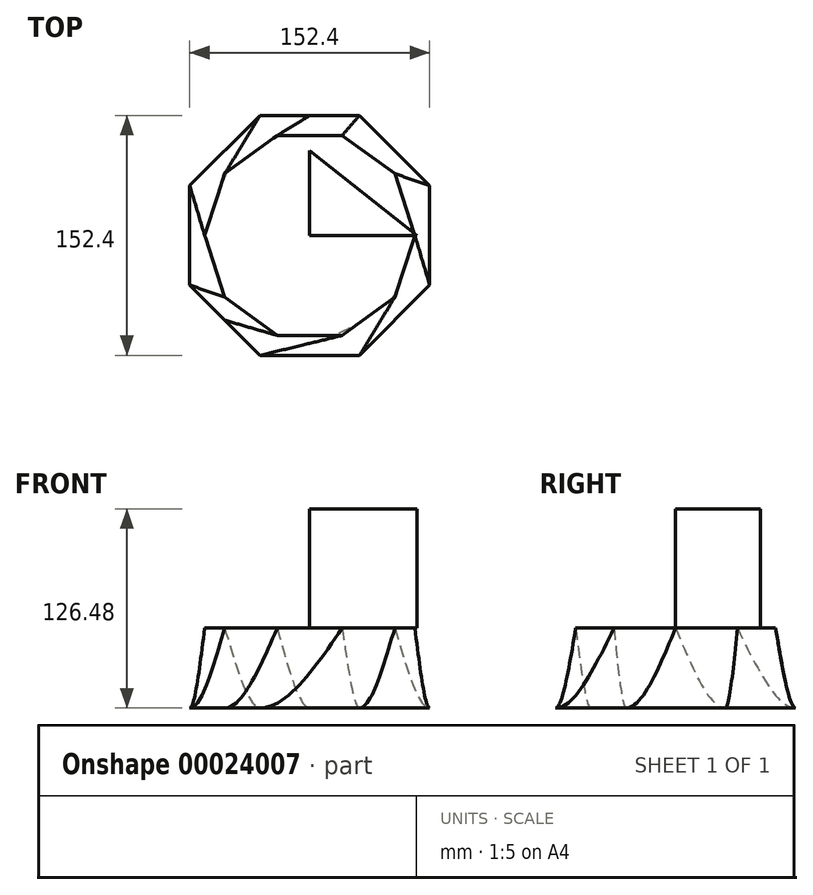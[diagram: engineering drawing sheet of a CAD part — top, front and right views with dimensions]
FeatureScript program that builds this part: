
annotation { "Feature Type Name" : "Feature", "Feature Type Description" : "" }
export const myFeature = defineFeature(function(context is Context, id is Id, definition is map)
    precondition{}
    {
        {
            var Q0;
            Q0=qCreatedBy(makeId("Top.planeOp"),FACE);
            var sketch = newSketch(context, id + "F0", { "sketchPlane" : qUnion([Q0])});
            skCircle(sketch, "E0.cCircle", {"center": v(0, 0) * mm, "radius": 76.2 * mm, "construction": true});
            skLineSegment(sketch, "E0.0", {"start": v(31.56, 76.2) * mm, "end": v(76.2, 31.56) * mm});
            skLineSegment(sketch, "E0.1", {"start": v(76.2, 31.56) * mm, "end": v(76.2, -31.56) * mm});
            skLineSegment(sketch, "E0.2", {"start": v(76.2, -31.56) * mm, "end": v(31.56, -76.2) * mm});
            skLineSegment(sketch, "E0.3", {"start": v(31.56, -76.2) * mm, "end": v(-31.56, -76.2) * mm});
            skLineSegment(sketch, "E0.4", {"start": v(-31.56, -76.2) * mm, "end": v(-76.2, -31.56) * mm});
            skLineSegment(sketch, "E0.5", {"start": v(-76.2, -31.56) * mm, "end": v(-76.2, 31.56) * mm});
            skLineSegment(sketch, "E0.6", {"start": v(-76.2, 31.56) * mm, "end": v(-31.56, 76.2) * mm});
            skLineSegment(sketch, "E0.7", {"start": v(-31.56, 76.2) * mm, "end": v(31.56, 76.2) * mm});
            skPoint(sketch, "E0.0.midPoint", {"position": v(53.88, 53.88) * mm});
            skSolve(sketch);
        }
        {
            var Q0;
            Q0 = qSketchRegion(id + "F0", true);
            var Q1;
            Q1=sQuery(id+"F0.wireOp",EDGE,"E0.6");
            var Q2;
            Q2=sQuery(id+"F0.wireOp",EDGE,"E0.7");
            var Q3;
            Q3=sQuery(id+"F0.wireOp",EDGE,"E0.0");
            var Q4;
            Q4=sQuery(id+"F0.wireOp",EDGE,"E0.5");
            var Q5;
            Q5=sQuery(id+"F0.wireOp",EDGE,"E0.4");
            var Q6;
            Q6=sQuery(id+"F0.wireOp",EDGE,"E0.3");
            var Q7;
            Q7=sQuery(id+"F0.wireOp",EDGE,"E0.2");
            var Q8;
            Q8=sQuery(id+"F0.wireOp",EDGE,"E0.1");
            extrude(context, id + "F1", {"entities" : qUnion([Q0]), "bodyType" : ToolBodyType.SURFACE, "surfaceEntities" : qUnion([Q1, Q2, Q3, Q4, Q5, Q6, Q7, Q8]), "oppositeDirection" : true, "depth" : 55.84 * mm, "hasDraft" : true, "draftAngle" : 3 * degree});
        }
        {
            var Q0;
            Q0=qCreatedBy(makeId("Top.planeOp"),FACE);
            cPlane(context, id + "F2", {"entities" : qUnion([Q0]), "cplaneType" : CPlaneType.OFFSET, "offset" : 50.8 * mm, "width" : 152.4 * mm, "height" : 152.4 * mm});
        }
        {
            var Q0;
            Q0=qCreatedBy(id+"F2.planeOp",FACE);
            var sketch = newSketch(context, id + "F3", { "sketchPlane" : qUnion([Q0])});
            skCircle(sketch, "E1.cCircle", {"center": v(0, 0) * mm, "radius": 63.5 * mm, "construction": true});
            skLineSegment(sketch, "E1.0", {"start": v(-66.77, 0) * mm, "end": v(-54.02, 39.25) * mm});
            skLineSegment(sketch, "E1.1", {"start": v(-54.02, 39.25) * mm, "end": v(-20.63, 63.5) * mm});
            skLineSegment(sketch, "E1.2", {"start": v(-20.63, 63.5) * mm, "end": v(20.63, 63.5) * mm});
            skLineSegment(sketch, "E1.3", {"start": v(20.63, 63.5) * mm, "end": v(54.02, 39.25) * mm});
            skLineSegment(sketch, "E1.4", {"start": v(54.02, 39.25) * mm, "end": v(66.77, 0) * mm});
            skLineSegment(sketch, "E1.5", {"start": v(66.77, 0) * mm, "end": v(54.02, -39.25) * mm});
            skLineSegment(sketch, "E1.6", {"start": v(54.02, -39.25) * mm, "end": v(20.63, -63.5) * mm});
            skLineSegment(sketch, "E1.7", {"start": v(20.63, -63.5) * mm, "end": v(-20.63, -63.5) * mm});
            skLineSegment(sketch, "E1.8", {"start": v(-20.63, -63.5) * mm, "end": v(-54.02, -39.25) * mm});
            skLineSegment(sketch, "E1.9", {"start": v(-54.02, -39.25) * mm, "end": v(-66.77, 0) * mm});
            skPoint(sketch, "E1.0.midPoint", {"position": v(-60.4, 19.62) * mm});
            skSolve(sketch);
        }
        {
            var Q0;
            Q0=qCreatedBy(makeId("Top.planeOp"),FACE);
            var sketch = newSketch(context, id + "F4", { "sketchPlane" : qUnion([Q0])});
            skCircle(sketch, "E2.cCircle", {"center": v(0, 0) * mm, "radius": 76.2 * mm, "construction": true});
            skLineSegment(sketch, "E2.0", {"start": v(31.56, 76.2) * mm, "end": v(76.2, 31.56) * mm});
            skLineSegment(sketch, "E2.1", {"start": v(76.2, 31.56) * mm, "end": v(76.2, -31.56) * mm});
            skLineSegment(sketch, "E2.2", {"start": v(76.2, -31.56) * mm, "end": v(31.56, -76.2) * mm});
            skLineSegment(sketch, "E2.3", {"start": v(31.56, -76.2) * mm, "end": v(-31.56, -76.2) * mm});
            skLineSegment(sketch, "E2.4", {"start": v(-31.56, -76.2) * mm, "end": v(-76.2, -31.56) * mm});
            skLineSegment(sketch, "E2.5", {"start": v(-76.2, -31.56) * mm, "end": v(-76.2, 31.56) * mm});
            skLineSegment(sketch, "E2.6", {"start": v(-76.2, 31.56) * mm, "end": v(-31.56, 76.2) * mm});
            skLineSegment(sketch, "E2.7", {"start": v(-31.56, 76.2) * mm, "end": v(31.56, 76.2) * mm});
            skPoint(sketch, "E2.0.midPoint", {"position": v(53.88, 53.88) * mm});
            skSolve(sketch);
        }
        {
            var Q0;
            Q0=makeQuery(id+"F3.imprint","IMPRINT",FACE,{"disambiguationData":[TD([[makeQuery(id+"F3.imprint","IMPRINT",EDGE,{"derivedFrom":sQuery(id+"F3.wireOp",EDGE,"E1.0")}),-1.0]])]});
            var Q1;
            Q1=makeQuery(id+"F4.imprint","IMPRINT",FACE,{"disambiguationData":[TD([[makeQuery(id+"F4.imprint","IMPRINT",EDGE,{"derivedFrom":sQuery(id+"F4.wireOp",EDGE,"E2.0")}),-1.0]])]});
            loft(context, id + "F5", {"endCondition" : LoftEndDerivativeType.TANGENT_TO_PROFILE, "endMagnitude" : 1, "sheetProfilesArray" : [{ "sheetProfileEntities" : qUnion([Q0]) }, { "sheetProfileEntities" : qUnion([Q1]) }]});
        }
        {
            var Q0;
            Q0=qCreatedBy(id+"F2.planeOp",FACE);
            var sketch = newSketch(context, id + "F6", { "sketchPlane" : qUnion([Q0])});
            skLineSegment(sketch, "E3", {"start": v(0, 0) * mm, "end": v(0, 53.82) * mm});
            skLineSegment(sketch, "E4", {"start": v(0, 53.82) * mm, "end": v(67.99, 0) * mm});
            skLineSegment(sketch, "E5", {"start": v(67.99, 0) * mm, "end": v(0, 0) * mm});
            skSolve(sketch);
        }
        {
            var Q0;
            Q0=makeQuery(id+"F6.imprint","IMPRINT",FACE,{"disambiguationData":[TD([[makeQuery(id+"F6.imprint","IMPRINT",EDGE,{"derivedFrom":sQuery(id+"F6.wireOp",EDGE,"E3")}),-1.0]])]});
            extrude(context, id + "F7", {"entities" : qUnion([Q0]), "operationType" : NewBodyOperationType.ADD, "depth" : 75.68 * mm});
        }
    });
